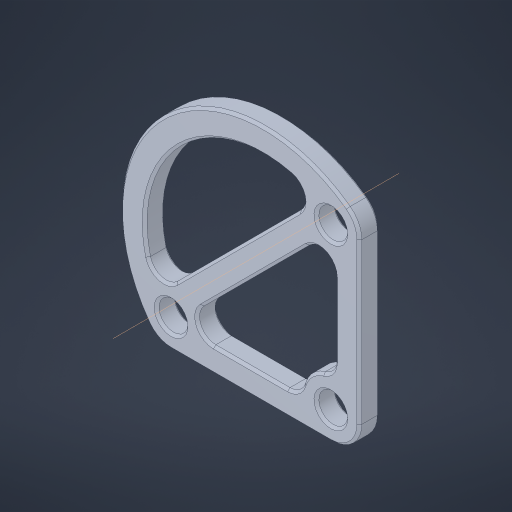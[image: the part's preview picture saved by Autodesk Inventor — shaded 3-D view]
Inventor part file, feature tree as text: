
AUTODESK INVENTOR PART (.ipt)
format: ipt  version: 2023.4 (Build 274418000, 418)  size: 251,904 bytes
history: native  units: in
note: dims shown in document units (in); Inventor stores cm internally (conversion verified against a paired STEP export)
features: plane x1, other x1
ambient origin geometry x8: Origin, YZ Plane, XZ Plane, XY Plane, X Axis, Y Axis, Z Axis, Center Point
bodies: Solid1 (feature_tree)
feature tree (2):
  plane  "Work Plane1"
  other  "MK4i Master Part_Default Falcon 500 Config"
